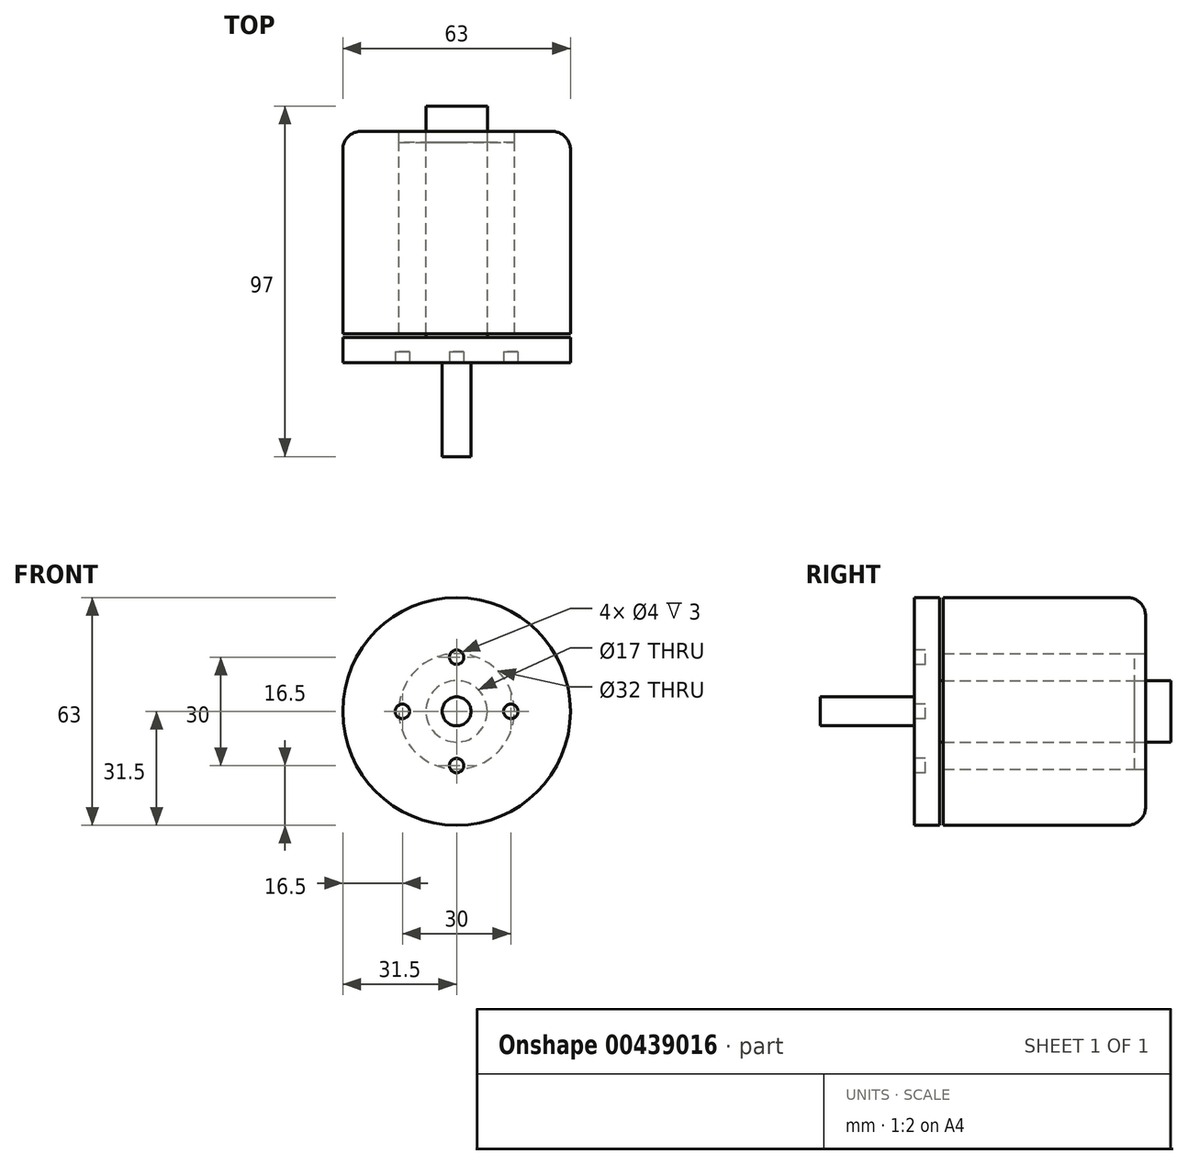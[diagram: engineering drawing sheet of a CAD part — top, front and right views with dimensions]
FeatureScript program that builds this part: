
annotation { "Feature Type Name" : "Feature", "Feature Type Description" : "" }
export const myFeature = defineFeature(function(context is Context, id is Id, definition is map)
    precondition{}
    {
        {
            var Q0;
            Q0=qCreatedBy(makeId("Front.planeOp"),FACE);
            var sketch = newSketch(context, id + "F0", { "sketchPlane" : qUnion([Q0])});
            skCircle(sketch, "E0", {"center": v(0, 0) * mm, "radius": 31.5 * mm});
            skCircle(sketch, "E1", {"center": v(0, 0) * mm, "radius": 8.5 * mm});
            skCircle(sketch, "E2", {"center": v(0, 0) * mm, "radius": 16 * mm});
            skCircle(sketch, "E3", {"center": v(0, 0) * mm, "radius": 4 * mm});
            skSolve(sketch);
        }
        {
            var Q0;
            Q0=makeQuery(id+"F0.imprint","IMPRINT",FACE,{"disambiguationData":[TD([[makeQuery(id+"F0.imprint","IMPRINT",EDGE,{"derivedFrom":sQuery(id+"F0.wireOp",EDGE,"E0")}),1.0]])]});
            extrude(context, id + "F1", {"entities" : qUnion([Q0]), "depth" : 56 * mm});
        }
        {
            var Q0;
            Q0=makeQuery(id+"F1.opExtrude","CAP_EDGE",EDGE,{"disambiguationData":[OSD([sQuery(id+"F0.wireOp",EDGE,"E0")])],"isStart":true});
            fillet(context, id + "F2", {"entities" : qUnion([Q0]), "radius" : 5 * mm, "tangentPropagation" : true, "allowEdgeOverflow" : false});
        }
        {
            var Q0;
            Q0=makeQuery(id+"F0.imprint","IMPRINT",FACE,{"disambiguationData":[TD([[makeQuery(id+"F0.imprint","IMPRINT",EDGE,{"derivedFrom":sQuery(id+"F0.wireOp",EDGE,"E1")}),1.0]])]});
            extrude(context, id + "F3", {"entities" : qUnion([Q0]), "operationType" : NewBodyOperationType.ADD, "depth" : 64 * mm, "hasSecondDirection" : true, "secondDirectionOppositeDirection" : true, "secondDirectionDepth" : 7 * mm});
        }
        {
            var Q0;
            Q0=makeQuery(id+"F0.imprint","IMPRINT",FACE,{"disambiguationData":[TD([[makeQuery(id+"F0.imprint","IMPRINT",EDGE,{"derivedFrom":sQuery(id+"F0.wireOp",EDGE,"E3")}),1.0]])]});
            extrude(context, id + "F4", {"entities" : qUnion([Q0]), "operationType" : NewBodyOperationType.ADD, "depth" : 90 * mm, "hasSecondDirection" : true, "secondDirectionOppositeDirection" : true, "secondDirectionDepth" : 7 * mm});
        }
        {
            var Q0;
            Q0=makeQuery(id+"F0.imprint","IMPRINT",FACE,{"disambiguationData":[TD([[makeQuery(id+"F0.imprint","IMPRINT",EDGE,{"derivedFrom":sQuery(id+"F0.wireOp",EDGE,"E1")}),-1.0]])]});
            extrude(context, id + "F5", {"entities" : qUnion([Q0]), "depth" : 3 * mm});
        }
        {
            var Q0;
            Q0 = qSketchRegion(id + "F0", true);
            var Q1;
            Q1=makeQuery(id+"F0.imprint","IMPRINT",FACE,{"disambiguationData":[TD([[makeQuery(id+"F0.imprint","IMPRINT",EDGE,{"derivedFrom":sQuery(id+"F0.wireOp",EDGE,"E1")}),-1.0]])]});
            extrude(context, id + "F6", {"entities" : qUnion([Q0, Q1]), "operationType" : NewBodyOperationType.ADD, "depth" : 64 * mm, "hasSecondDirection" : true, "secondDirectionOppositeDirection" : false, "secondDirectionDepth" : 57 * mm});
        }
        {
            var Q0;
            Q0=makeQuery(id+"F6.opExtrude","CAP_FACE",FACE,{"disambiguationData":[OSD([sQuery(id+"F0.wireOp",EDGE,"E0"),sQuery(id+"F0.wireOp",EDGE,"E1")])],"isStart":false});
            var sketch = newSketch(context, id + "F7", { "sketchPlane" : qUnion([Q0])});
            skCircle(sketch, "E4", {"center": v(0, 0) * mm, "radius": 15 * mm, "construction": true});
            skCircle(sketch, "E5", {"center": v(0, 15) * mm, "radius": 2 * mm});
            skCircle(sketch, "E6.1.0", {"center": v(-15, 0) * mm, "radius": 2 * mm});
            skCircle(sketch, "E6.2.0", {"center": v(0, -15) * mm, "radius": 2 * mm});
            skCircle(sketch, "E6.3.0", {"center": v(15, 0) * mm, "radius": 2 * mm});
            skSolve(sketch);
        }
        {
            var Q0;
            Q0 = qSketchRegion(id + "F7", true);
            extrude(context, id + "F8", {"entities" : qUnion([Q0]), "operationType" : NewBodyOperationType.REMOVE, "oppositeDirection" : true, "depth" : 3 * mm});
        }
    });
